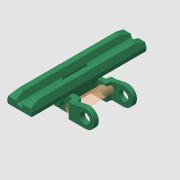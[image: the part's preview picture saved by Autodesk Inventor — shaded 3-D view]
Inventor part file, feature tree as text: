
AUTODESK INVENTOR PART (.ipt)
format: ipt  version: 2021 (Build 250183000, 183)  size: 891,904 bytes
history: native  units: in
note: dims shown in document units (in); Inventor stores cm internally (conversion verified against a paired STEP export)
features: other x4, sketch x3, extrude x3, imported_body x1
ambient origin geometry x8: Origin, YZ Plane, XZ Plane, XY Plane, X Axis, Y Axis, Z Axis, Center Point
bodies: Body1 (feature_tree), Body2 (feature_tree), Body3 (feature_tree), Body4 (feature_tree)
feature tree (11):
  parser-record x1  (decoder bookkeeping rows leaked as tree rows — omitted from the tree; the rows remain in map.json)
  imported_body  "Base1"
  sketch  "Sketch1"  dims[d0=0.118in d1=0.063in d2=0.0in]
  other  "Srf1"
  sketch  "Sketch2"  dims[d3=0.0in d4=0.118in]
  other  "Srf2"
  sketch  "Sketch3"  dims[d5=0.063in d6=0.0in d7=0.0in d8=0.0in d9=0.0in d10=0.125in d11=1.0in d12=0.0in]
  other  "Srf3"
  extrude  "ExtrusionSrf1"  Depth=0.063in TaperAngle=0.0deg
  extrude  "ExtrusionSrf2"  Depth=0.118in
  extrude  "ExtrusionSrf3"  TaperAngle=0.0deg  [1 undecoded]
note: 1 required parameter value undecoded (feature->parameter linkage not recoverable at this tier; creation-order binding heuristic only, values carry confidence <= 0.55)
